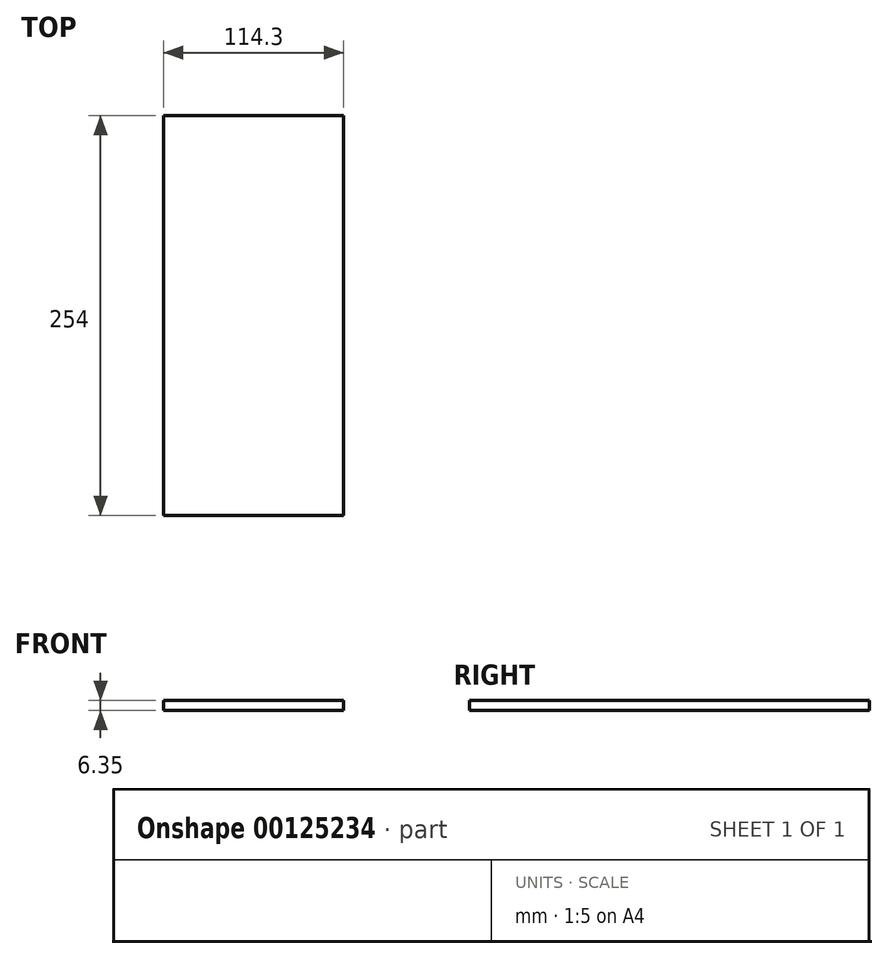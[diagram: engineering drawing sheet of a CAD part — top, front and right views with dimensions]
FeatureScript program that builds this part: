
annotation { "Feature Type Name" : "Feature", "Feature Type Description" : "" }
export const myFeature = defineFeature(function(context is Context, id is Id, definition is map)
    precondition{}
    {
        {
            var Q0;
            Q0=qCreatedBy(makeId("Top.planeOp"),FACE);
            var sketch = newSketch(context, id + "F0", { "sketchPlane" : qUnion([Q0])});
            skLineSegment(sketch, "E0.bottom", {"start": v(57.15, 127) * mm, "end": v(-57.15, 127) * mm});
            skLineSegment(sketch, "E0.top", {"start": v(57.15, -127) * mm, "end": v(-57.15, -127) * mm});
            skLineSegment(sketch, "E0.left", {"start": v(57.15, 127) * mm, "end": v(57.15, -127) * mm});
            skLineSegment(sketch, "E0.right", {"start": v(-57.15, 127) * mm, "end": v(-57.15, -127) * mm});
            skPoint(sketch, "E0.middle", {"position": v(0, 0) * mm});
            skSolve(sketch);
        }
        {
            var Q0;
            Q0=makeQuery(id+"F0.imprint","IMPRINT",FACE,{"disambiguationData":[TD([[makeQuery(id+"F0.imprint","IMPRINT",EDGE,{"derivedFrom":sQuery(id+"F0.wireOp",EDGE,"E0.bottom")}),1.0]])]});
            var Q1;
            Q1 = qSketchRegion(id + "F0", true);
            extrude(context, id + "F1", {"entities" : qUnion([Q0, Q1]), "depth" : 6.35 * mm});
        }
    });
